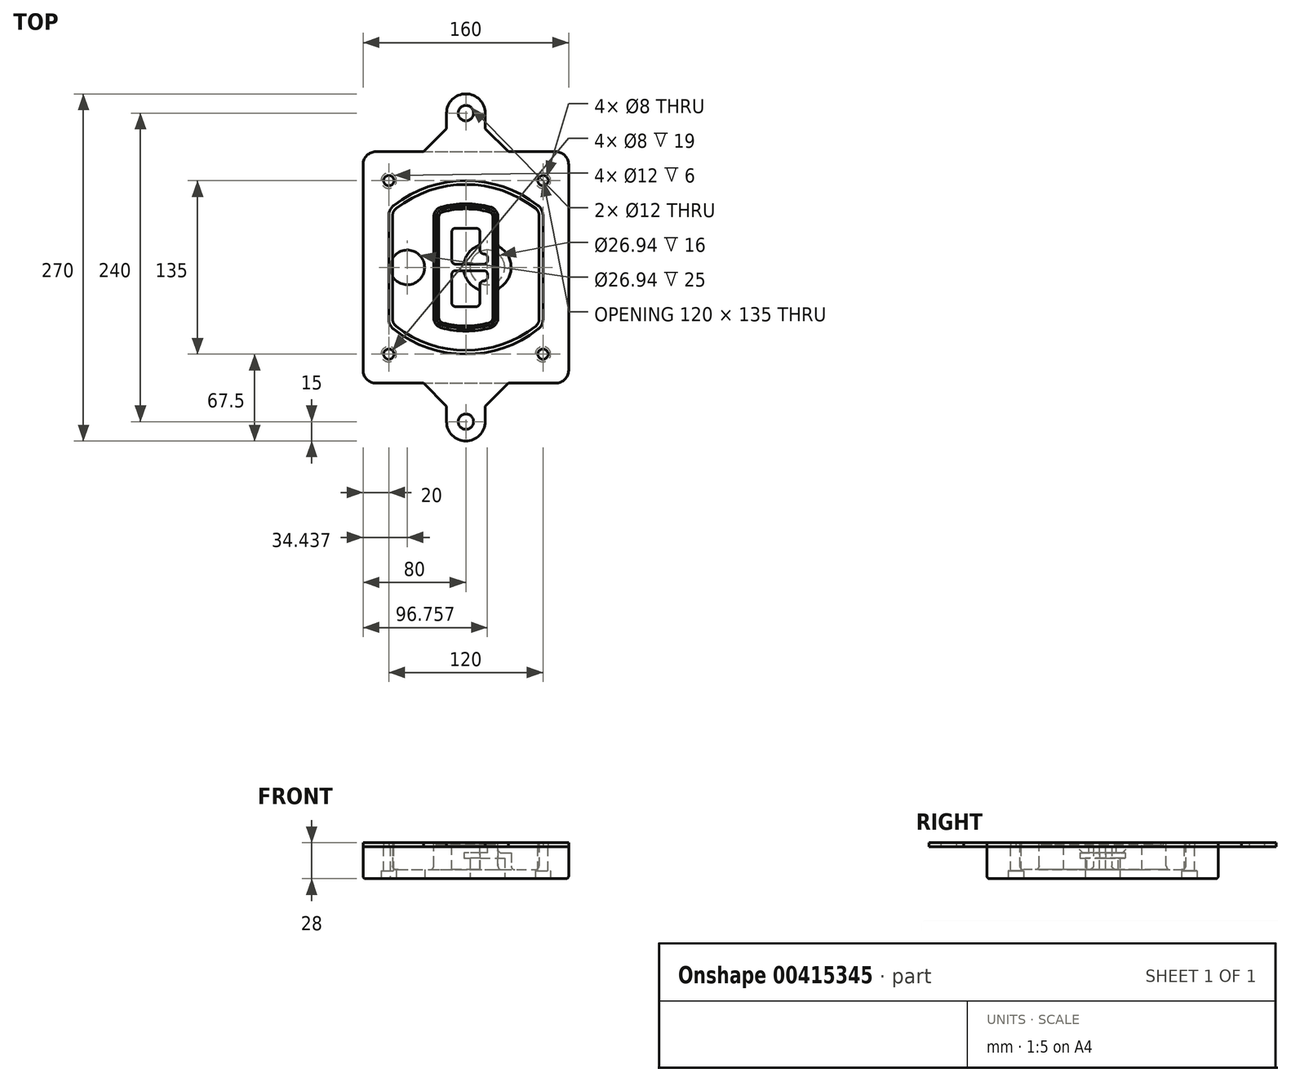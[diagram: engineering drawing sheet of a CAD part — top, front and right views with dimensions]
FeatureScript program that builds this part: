
annotation { "Feature Type Name" : "Feature", "Feature Type Description" : "" }
export const myFeature = defineFeature(function(context is Context, id is Id, definition is map)
    precondition{}
    {
        {
            var Q0;
            Q0=qCreatedBy(makeId("Top.planeOp"),FACE);
            var sketch = newSketch(context, id + "F0", { "sketchPlane" : qUnion([Q0])});
            skPoint(sketch, "E0.rect.middle", {"position": v(0, 0) * mm});
            skLineSegment(sketch, "E1.bottom", {"start": v(-70, -90) * mm, "end": v(70, -90) * mm});
            skLineSegment(sketch, "E1.top", {"start": v(-70, 90) * mm, "end": v(70, 90) * mm});
            skLineSegment(sketch, "E1.left", {"start": v(-80, -80) * mm, "end": v(-80, 80) * mm});
            skLineSegment(sketch, "E1.right", {"start": v(80, -80) * mm, "end": v(80, 80) * mm});
            skLineSegment(sketch, "E2", {"start": v(-80, 90) * mm, "end": v(80, -90) * mm, "construction": true});
            skLineSegment(sketch, "E3", {"start": v(80, 90) * mm, "end": v(-80, -90) * mm, "construction": true});
            skCircle(sketch, "E4", {"center": v(-60, 67.5) * mm, "radius": 4 * mm});
            skCircle(sketch, "E5", {"center": v(60, 67.5) * mm, "radius": 4 * mm});
            skCircle(sketch, "E6", {"center": v(60, -67.5) * mm, "radius": 4 * mm});
            skCircle(sketch, "E7", {"center": v(-60, -67.5) * mm, "radius": 4 * mm});
            skLineSegment(sketch, "E8", {"start": v(-60, 67.5) * mm, "end": v(60, 67.5) * mm, "construction": true});
            skLineSegment(sketch, "E9", {"start": v(60, 67.5) * mm, "end": v(60, -67.5) * mm, "construction": true});
            skLineSegment(sketch, "E10", {"start": v(60, -67.5) * mm, "end": v(-60, -67.5) * mm, "construction": true});
            skLineSegment(sketch, "E11", {"start": v(-60, -67.5) * mm, "end": v(-60, 67.5) * mm, "construction": true});
            skLineSegment(sketch, "E12", {"start": v(-60, 40.3) * mm, "end": v(-60, -40.3) * mm});
            skLineSegment(sketch, "E13", {"start": v(60, 40.3) * mm, "end": v(60, -40.3) * mm});
            skArc(sketch, "E14", {"start": v(56.15, 48.18) * mm, "mid": v(0, 67.5) * mm, "end": v(-56.15, 48.18) * mm});
            skArc(sketch, "E15", {"start": v(-56.15, -48.18) * mm, "mid": v(0, -67.5) * mm, "end": v(56.15, -48.18) * mm});
            skLineSegment(sketch, "E16", {"start": v(-60, 0) * mm, "end": v(60, 0) * mm, "construction": true});
            skPoint(sketch, "E17.visualSharp", {"position": v(-60, -45) * mm});
            skArc(sketch, "E17.filletArc", {"start": v(-60, -40.3) * mm, "mid": v(-58.99, -44.68) * mm, "end": v(-56.15, -48.18) * mm});
            skPoint(sketch, "E18.visualSharp", {"position": v(-60, 45) * mm});
            skArc(sketch, "E18.filletArc", {"start": v(-56.15, 48.18) * mm, "mid": v(-58.99, 44.68) * mm, "end": v(-60, 40.3) * mm});
            skPoint(sketch, "E19.visualSharp", {"position": v(60, 45) * mm});
            skArc(sketch, "E19.filletArc", {"start": v(60, 40.3) * mm, "mid": v(58.99, 44.68) * mm, "end": v(56.15, 48.18) * mm});
            skPoint(sketch, "E20.visualSharp", {"position": v(60, -45) * mm});
            skArc(sketch, "E20.filletArc", {"start": v(56.15, -48.18) * mm, "mid": v(58.99, -44.68) * mm, "end": v(60, -40.3) * mm});
            skPoint(sketch, "E21.visualSharp", {"position": v(-80, 90) * mm});
            skArc(sketch, "E21.filletArc", {"start": v(-70, 90) * mm, "mid": v(-77.07, 87.07) * mm, "end": v(-80, 80) * mm});
            skPoint(sketch, "E22.visualSharp", {"position": v(80, 90) * mm});
            skArc(sketch, "E22.filletArc", {"start": v(80, 80) * mm, "mid": v(77.07, 87.07) * mm, "end": v(70, 90) * mm});
            skPoint(sketch, "E23.visualSharp", {"position": v(80, -90) * mm});
            skArc(sketch, "E23.filletArc", {"start": v(70, -90) * mm, "mid": v(77.07, -87.07) * mm, "end": v(80, -80) * mm});
            skPoint(sketch, "E24.visualSharp", {"position": v(-80, -90) * mm});
            skArc(sketch, "E24.filletArc", {"start": v(-80, -80) * mm, "mid": v(-77.07, -87.07) * mm, "end": v(-70, -90) * mm});
            skArc(sketch, "E25.0", {"start": v(57, 40.3) * mm, "mid": v(56.3, 43.36) * mm, "end": v(54.3, 45.81) * mm});
            skLineSegment(sketch, "E25.1", {"start": v(57, 40.3) * mm, "end": v(57, -40.3) * mm});
            skArc(sketch, "E25.2", {"start": v(54.3, -45.81) * mm, "mid": v(56.3, -43.36) * mm, "end": v(57, -40.3) * mm});
            skArc(sketch, "E25.3", {"start": v(-54.3, -45.81) * mm, "mid": v(0, -64.5) * mm, "end": v(54.3, -45.81) * mm});
            skArc(sketch, "E25.4", {"start": v(-57, -40.3) * mm, "mid": v(-56.3, -43.36) * mm, "end": v(-54.3, -45.81) * mm});
            skArc(sketch, "E25.5", {"start": v(54.3, 45.81) * mm, "mid": v(0, 64.5) * mm, "end": v(-54.3, 45.81) * mm});
            skLineSegment(sketch, "E25.6", {"start": v(-57, 40.3) * mm, "end": v(-57, -40.3) * mm});
            skArc(sketch, "E25.7", {"start": v(-54.3, 45.81) * mm, "mid": v(-56.3, 43.36) * mm, "end": v(-57, 40.3) * mm});
            skArc(sketch, "E26.0", {"start": v(-58.62, 51.33) * mm, "mid": v(-62.58, 46.43) * mm, "end": v(-64, 40.3) * mm});
            skArc(sketch, "E26.1", {"start": v(58.62, 51.33) * mm, "mid": v(0, 71.5) * mm, "end": v(-58.62, 51.33) * mm});
            skArc(sketch, "E26.2", {"start": v(64, 40.3) * mm, "mid": v(62.58, 46.43) * mm, "end": v(58.62, 51.33) * mm});
            skLineSegment(sketch, "E26.3", {"start": v(64, 40.3) * mm, "end": v(64, -40.3) * mm});
            skArc(sketch, "E26.4", {"start": v(58.62, -51.33) * mm, "mid": v(62.58, -46.43) * mm, "end": v(64, -40.3) * mm});
            skLineSegment(sketch, "E26.5", {"start": v(-64, 40.3) * mm, "end": v(-64, -40.3) * mm});
            skArc(sketch, "E26.6", {"start": v(-58.62, -51.33) * mm, "mid": v(0, -71.5) * mm, "end": v(58.62, -51.33) * mm});
            skArc(sketch, "E26.7", {"start": v(-64, -40.3) * mm, "mid": v(-62.58, -46.43) * mm, "end": v(-58.62, -51.33) * mm});
            skSolve(sketch);
        }
        {
            var Q0;
            Q0=makeQuery(id+"F0.imprint","IMPRINT",FACE,{"disambiguationData":[TD([[makeQuery(id+"F0.imprint","IMPRINT",EDGE,{"derivedFrom":sQuery(id+"F0.wireOp",EDGE,"E1.bottom")}),1.0]])]});
            var Q1;
            Q1=makeQuery(id+"F0.imprint","IMPRINT",FACE,{"disambiguationData":[TD([[makeQuery(id+"F0.imprint","IMPRINT",EDGE,{"derivedFrom":sQuery(id+"F0.wireOp",EDGE,"E12")}),1.0]])]});
            var Q2;
            Q2=makeQuery(id+"F0.imprint","IMPRINT",FACE,{"disambiguationData":[TD([[makeQuery(id+"F0.imprint","IMPRINT",EDGE,{"derivedFrom":sQuery(id+"F0.wireOp",EDGE,"E25.0")}),1.0]])]});
            var Q3;
            Q3=makeQuery(id+"F0.imprint","IMPRINT",FACE,{"disambiguationData":[TD([[makeQuery(id+"F0.imprint","IMPRINT",EDGE,{"derivedFrom":sQuery(id+"F0.wireOp",EDGE,"E12")}),-1.0]])]});
            extrude(context, id + "F1", {"entities" : qUnion([Q0, Q1, Q2, Q3]), "oppositeDirection" : true, "depth" : 25 * mm});
        }
        {
            var Q0;
            Q0=makeQuery(id+"F0.imprint","IMPRINT",FACE,{"disambiguationData":[TD([[makeQuery(id+"F0.imprint","IMPRINT",EDGE,{"derivedFrom":sQuery(id+"F0.wireOp",EDGE,"E12")}),1.0]])]});
            extrude(context, id + "F2", {"entities" : qUnion([Q0]), "operationType" : NewBodyOperationType.ADD, "depth" : 3 * mm});
        }
        {
            var Q0;
            Q0=makeQuery(id+"F0.imprint","IMPRINT",FACE,{"disambiguationData":[TD([[makeQuery(id+"F0.imprint","IMPRINT",EDGE,{"derivedFrom":sQuery(id+"F0.wireOp",EDGE,"E25.0")}),1.0]])]});
            extrude(context, id + "F3", {"entities" : qUnion([Q0]), "operationType" : NewBodyOperationType.REMOVE, "oppositeDirection" : true, "depth" : 18 * mm});
        }
        {
            var Q0;
            Q0=makeQuery(id+"F2.opExtrude","CAP_FACE",FACE,{"disambiguationData":[OSD([sQuery(id+"F0.wireOp",EDGE,"E12"),sQuery(id+"F0.wireOp",EDGE,"E13"),sQuery(id+"F0.wireOp",EDGE,"E14"),sQuery(id+"F0.wireOp",EDGE,"E15"),sQuery(id+"F0.wireOp",EDGE,"E17.filletArc"),sQuery(id+"F0.wireOp",EDGE,"E18.filletArc"),sQuery(id+"F0.wireOp",EDGE,"E19.filletArc"),sQuery(id+"F0.wireOp",EDGE,"E20.filletArc"),sQuery(id+"F0.wireOp",EDGE,"E25.0"),sQuery(id+"F0.wireOp",EDGE,"E25.1"),sQuery(id+"F0.wireOp",EDGE,"E25.2"),sQuery(id+"F0.wireOp",EDGE,"E25.3"),sQuery(id+"F0.wireOp",EDGE,"E25.4"),sQuery(id+"F0.wireOp",EDGE,"E25.5"),sQuery(id+"F0.wireOp",EDGE,"E25.6"),sQuery(id+"F0.wireOp",EDGE,"E25.7")])],"isStart":false});
            var sketch = newSketch(context, id + "F4", { "sketchPlane" : qUnion([Q0])});
            skArc(sketch, "E27.0", {"start": v(-19.08, -46.97) * mm, "mid": v(0, -49.5) * mm, "end": v(19.08, -46.97) * mm});
            skArc(sketch, "E28.0", {"start": v(19.08, 46.97) * mm, "mid": v(0, 49.5) * mm, "end": v(-19.08, 46.97) * mm});
            skLineSegment(sketch, "E29", {"start": v(-25, 39.25) * mm, "end": v(-25, -39.25) * mm});
            skLineSegment(sketch, "E30", {"start": v(25, 39.25) * mm, "end": v(25, -39.25) * mm});
            skLineSegment(sketch, "E31", {"start": v(-25, 45.1) * mm, "end": v(25, 45.1) * mm, "construction": true});
            skLineSegment(sketch, "E32", {"start": v(-25, -45.1) * mm, "end": v(25, -45.1) * mm, "construction": true});
            skPoint(sketch, "E33.visualSharp", {"position": v(-25, 45.1) * mm});
            skArc(sketch, "E33.filletArc", {"start": v(-19.08, 46.97) * mm, "mid": v(-23.35, 44.11) * mm, "end": v(-25, 39.25) * mm});
            skPoint(sketch, "E34.visualSharp", {"position": v(25, 45.1) * mm});
            skArc(sketch, "E34.filletArc", {"start": v(25, 39.25) * mm, "mid": v(23.35, 44.11) * mm, "end": v(19.08, 46.97) * mm});
            skPoint(sketch, "E35.visualSharp", {"position": v(25, -45.1) * mm});
            skArc(sketch, "E35.filletArc", {"start": v(19.08, -46.97) * mm, "mid": v(23.35, -44.11) * mm, "end": v(25, -39.25) * mm});
            skPoint(sketch, "E36.visualSharp", {"position": v(-25, -45.1) * mm});
            skArc(sketch, "E36.filletArc", {"start": v(-25, -39.25) * mm, "mid": v(-23.35, -44.11) * mm, "end": v(-19.08, -46.97) * mm});
            skArc(sketch, "E37.0", {"start": v(54.3, 45.81) * mm, "mid": v(0, 64.5) * mm, "end": v(-54.3, 45.81) * mm});
            skArc(sketch, "E37.1", {"start": v(-54.3, 45.81) * mm, "mid": v(-56.3, 43.36) * mm, "end": v(-57, 40.3) * mm});
            skLineSegment(sketch, "E37.2", {"start": v(-57, 40.3) * mm, "end": v(-57, -40.3) * mm});
            skArc(sketch, "E37.3", {"start": v(-57, -40.3) * mm, "mid": v(-56.3, -43.36) * mm, "end": v(-54.3, -45.81) * mm});
            skArc(sketch, "E37.4", {"start": v(-54.3, -45.81) * mm, "mid": v(0, -64.5) * mm, "end": v(54.3, -45.81) * mm});
            skArc(sketch, "E37.5", {"start": v(54.3, -45.81) * mm, "mid": v(56.3, -43.36) * mm, "end": v(57, -40.3) * mm});
            skLineSegment(sketch, "E37.6", {"start": v(57, 40.3) * mm, "end": v(57, -40.3) * mm});
            skArc(sketch, "E37.7", {"start": v(57, 40.3) * mm, "mid": v(56.3, 43.36) * mm, "end": v(54.3, 45.81) * mm});
            skLineSegment(sketch, "E38.0", {"start": v(23, 39.25) * mm, "end": v(23, -39.25) * mm});
            skArc(sketch, "E38.1", {"start": v(18.56, -45.04) * mm, "mid": v(21.76, -42.9) * mm, "end": v(23, -39.25) * mm});
            skArc(sketch, "E38.2", {"start": v(-18.56, -45.04) * mm, "mid": v(0, -47.5) * mm, "end": v(18.56, -45.04) * mm});
            skArc(sketch, "E38.3", {"start": v(-23, -39.25) * mm, "mid": v(-21.76, -42.9) * mm, "end": v(-18.56, -45.04) * mm});
            skLineSegment(sketch, "E38.4", {"start": v(-23, 39.25) * mm, "end": v(-23, -39.25) * mm});
            skArc(sketch, "E38.5", {"start": v(23, 39.25) * mm, "mid": v(21.76, 42.9) * mm, "end": v(18.56, 45.04) * mm});
            skArc(sketch, "E38.6", {"start": v(-18.56, 45.04) * mm, "mid": v(-21.76, 42.9) * mm, "end": v(-23, 39.25) * mm});
            skArc(sketch, "E38.7", {"start": v(18.56, 45.04) * mm, "mid": v(0, 47.5) * mm, "end": v(-18.56, 45.04) * mm});
            skArc(sketch, "E39.0", {"start": v(21, 39.25) * mm, "mid": v(20.18, 41.68) * mm, "end": v(18.04, 43.1) * mm});
            skLineSegment(sketch, "E39.1", {"start": v(21, 39.25) * mm, "end": v(21, -39.25) * mm});
            skArc(sketch, "E39.2", {"start": v(18.04, -43.1) * mm, "mid": v(20.18, -41.68) * mm, "end": v(21, -39.25) * mm});
            skArc(sketch, "E39.3", {"start": v(-18.04, -43.1) * mm, "mid": v(0, -45.5) * mm, "end": v(18.04, -43.1) * mm});
            skArc(sketch, "E39.4", {"start": v(-21, -39.25) * mm, "mid": v(-20.18, -41.68) * mm, "end": v(-18.04, -43.1) * mm});
            skArc(sketch, "E39.5", {"start": v(18.04, 43.1) * mm, "mid": v(0, 45.5) * mm, "end": v(-18.04, 43.1) * mm});
            skLineSegment(sketch, "E39.6", {"start": v(-21, 39.25) * mm, "end": v(-21, -39.25) * mm});
            skArc(sketch, "E39.7", {"start": v(-18.04, 43.1) * mm, "mid": v(-20.18, 41.68) * mm, "end": v(-21, 39.25) * mm});
            skLineSegment(sketch, "E40", {"start": v(-25, 0) * mm, "end": v(25, 0) * mm, "construction": true});
            skLineSegment(sketch, "E41", {"start": v(-11, 5.5) * mm, "end": v(-11, 27.5) * mm});
            skLineSegment(sketch, "E42", {"start": v(-8, 30.5) * mm, "end": v(8, 30.5) * mm});
            skLineSegment(sketch, "E43", {"start": v(11, 27.5) * mm, "end": v(11, 13.5) * mm});
            skLineSegment(sketch, "E44", {"start": v(14, 10.5) * mm, "end": v(14, 10.5) * mm});
            skLineSegment(sketch, "E45", {"start": v(17, 7.5) * mm, "end": v(17, 5.5) * mm});
            skLineSegment(sketch, "E46", {"start": v(14, 2.5) * mm, "end": v(-8, 2.5) * mm});
            skPoint(sketch, "E47.visualSharp", {"position": v(-11, 30.5) * mm});
            skArc(sketch, "E47.filletArc", {"start": v(-8, 30.5) * mm, "mid": v(-10.12, 29.62) * mm, "end": v(-11, 27.5) * mm});
            skPoint(sketch, "E48.visualSharp", {"position": v(11, 30.5) * mm});
            skArc(sketch, "E48.filletArc", {"start": v(11, 27.5) * mm, "mid": v(10.12, 29.62) * mm, "end": v(8, 30.5) * mm});
            skPoint(sketch, "E49.visualSharp", {"position": v(11, 10.5) * mm});
            skArc(sketch, "E49.filletArc", {"start": v(11, 13.5) * mm, "mid": v(11.88, 11.38) * mm, "end": v(14, 10.5) * mm});
            skPoint(sketch, "E50.visualSharp", {"position": v(17, 10.5) * mm});
            skArc(sketch, "E50.filletArc", {"start": v(17, 7.5) * mm, "mid": v(16.12, 9.62) * mm, "end": v(14, 10.5) * mm});
            skPoint(sketch, "E51.visualSharp", {"position": v(17, 2.5) * mm});
            skArc(sketch, "E51.filletArc", {"start": v(14, 2.5) * mm, "mid": v(16.12, 3.38) * mm, "end": v(17, 5.5) * mm});
            skPoint(sketch, "E52.visualSharp", {"position": v(-11, 2.5) * mm});
            skArc(sketch, "E52.filletArc", {"start": v(-11, 5.5) * mm, "mid": v(-10.12, 3.38) * mm, "end": v(-8, 2.5) * mm});
            skLineSegment(sketch, "E53.0.MirrorCS", {"start": v(14, -2.5) * mm, "end": v(-8, -2.5) * mm});
            skArc(sketch, "E54.0.MirrorCS", {"start": v(-11, -5.5) * mm, "mid": v(-10.12, -3.38) * mm, "end": v(-8, -2.5) * mm});
            skLineSegment(sketch, "E55.0.MirrorCS", {"start": v(-11, -5.5) * mm, "end": v(-11, -27.5) * mm});
            skArc(sketch, "E56.0.MirrorCS", {"start": v(-8, -30.5) * mm, "mid": v(-10.12, -29.62) * mm, "end": v(-11, -27.5) * mm});
            skLineSegment(sketch, "E57.0.MirrorCS", {"start": v(-8, -30.5) * mm, "end": v(8, -30.5) * mm});
            skArc(sketch, "E58.0.MirrorCS", {"start": v(11, -27.5) * mm, "mid": v(10.12, -29.62) * mm, "end": v(8, -30.5) * mm});
            skLineSegment(sketch, "E59.0.MirrorCS", {"start": v(11, -27.5) * mm, "end": v(11, -13.5) * mm});
            skArc(sketch, "E60.0.MirrorCS", {"start": v(11, -13.5) * mm, "mid": v(11.88, -11.38) * mm, "end": v(14, -10.5) * mm});
            skArc(sketch, "E61.0.MirrorCS", {"start": v(17, -7.5) * mm, "mid": v(16.12, -9.62) * mm, "end": v(14, -10.5) * mm});
            skLineSegment(sketch, "E62.0.MirrorCS", {"start": v(17, -7.5) * mm, "end": v(17, -5.5) * mm});
            skArc(sketch, "E63.0.MirrorCS", {"start": v(14, -2.5) * mm, "mid": v(16.12, -3.38) * mm, "end": v(17, -5.5) * mm});
            skSolve(sketch);
        }
        {
            var Q0;
            Q0=makeQuery(id+"F4.imprint","IMPRINT",FACE,{"disambiguationData":[TD([[makeQuery(id+"F4.imprint","IMPRINT",EDGE,{"derivedFrom":sQuery(id+"F4.wireOp",EDGE,"E27.0")}),1.0]])]});
            var Q1;
            Q1=makeQuery(id+"F4.imprint","IMPRINT",FACE,{"disambiguationData":[TD([[makeQuery(id+"F4.imprint","IMPRINT",EDGE,{"derivedFrom":sQuery(id+"F4.wireOp",EDGE,"E38.0")}),-1.0]])]});
            var Q2;
            Q2=makeQuery(id+"F4.imprint","IMPRINT",FACE,{"disambiguationData":[TD([[makeQuery(id+"F4.imprint","IMPRINT",EDGE,{"derivedFrom":sQuery(id+"F4.wireOp",EDGE,"E39.0")}),1.0]])]});
            extrude(context, id + "F5", {"entities" : qUnion([Q0, Q1, Q2]), "operationType" : NewBodyOperationType.ADD, "endBound" : BoundingType.UP_TO_NEXT, "oppositeDirection" : true, "depth" : 25 * mm});
        }
        {
            var Q0;
            Q0=makeQuery(id+"F4.imprint","IMPRINT",FACE,{"disambiguationData":[TD([[makeQuery(id+"F4.imprint","IMPRINT",EDGE,{"derivedFrom":sQuery(id+"F4.wireOp",EDGE,"E38.0")}),-1.0]])]});
            extrude(context, id + "F6", {"entities" : qUnion([Q0]), "operationType" : NewBodyOperationType.REMOVE, "oppositeDirection" : true, "depth" : 2 * mm});
        }
        {
            var Q0;
            Q0=makeQuery(id+"F1.opExtrude","CAP_FACE",FACE,{"disambiguationData":[OSD([sQuery(id+"F0.wireOp",EDGE,"E1.bottom"),sQuery(id+"F0.wireOp",EDGE,"E1.top"),sQuery(id+"F0.wireOp",EDGE,"E1.left"),sQuery(id+"F0.wireOp",EDGE,"E1.right"),sQuery(id+"F0.wireOp",EDGE,"E4"),sQuery(id+"F0.wireOp",EDGE,"E5"),sQuery(id+"F0.wireOp",EDGE,"E6"),sQuery(id+"F0.wireOp",EDGE,"E7"),sQuery(id+"F0.wireOp",EDGE,"E21.filletArc"),sQuery(id+"F0.wireOp",EDGE,"E22.filletArc"),sQuery(id+"F0.wireOp",EDGE,"E23.filletArc"),sQuery(id+"F0.wireOp",EDGE,"E24.filletArc")])],"isStart":false});
            var sketch = newSketch(context, id + "F7", { "sketchPlane" : qUnion([Q0])});
            skCircle(sketch, "E64", {"center": v(16.76, 0) * mm, "radius": 13.47 * mm});
            skCircle(sketch, "E65", {"center": v(-45.56, 0) * mm, "radius": 13.47 * mm});
            skLineSegment(sketch, "E66", {"start": v(80, 0) * mm, "end": v(-80, 0) * mm});
            skCircle(sketch, "E67", {"center": v(16.76, 0) * mm, "radius": 18.47 * mm});
            skCircle(sketch, "E68", {"center": v(60, -67.5) * mm, "radius": 6 * mm});
            skCircle(sketch, "E69", {"center": v(-60, -67.5) * mm, "radius": 6 * mm});
            skCircle(sketch, "E70", {"center": v(-60, 67.5) * mm, "radius": 6 * mm});
            skCircle(sketch, "E71", {"center": v(60, 67.5) * mm, "radius": 6 * mm});
            skSolve(sketch);
        }
        {
            var Q0;
            {var subQ1=sQuery(id+"F7.wireOp",EDGE,"E66");var subQ4=sQuery(id+"F7.wireOp",EDGE,"E64");var subQ6=makeQuery(id+"F7.imprint","INTERSECT",VERTEX,{"disambiguationData":[OD(0.0)],"derivedFrom":[subQ4,subQ1]});Q0=makeQuery(id+"F7.imprint","IMPRINT",FACE,{"disambiguationData":[TD([[makeQuery(id+"F7.imprint","IMPRINT",EDGE,{"disambiguationData":[TD([[subQ6,-1.0]])],"derivedFrom":subQ4}),-1.0]])]});}
            var Q1;
            {var subQ0=sQuery(id+"F7.wireOp",EDGE,"E66");var subQ1=sQuery(id+"F7.wireOp",EDGE,"E64");var subQ3=makeQuery(id+"F7.imprint","INTERSECT",VERTEX,{"disambiguationData":[OD(0.0)],"derivedFrom":[subQ1,subQ0]});Q1=makeQuery(id+"F7.imprint","IMPRINT",FACE,{"disambiguationData":[TD([[makeQuery(id+"F7.imprint","IMPRINT",EDGE,{"disambiguationData":[TD([[subQ3,-1.0]])],"derivedFrom":subQ1}),1.0]])]});}
            var Q2;
            {var subQ0=sQuery(id+"F7.wireOp",EDGE,"E66");var subQ1=sQuery(id+"F7.wireOp",EDGE,"E64");var subQ3=makeQuery(id+"F7.imprint","INTERSECT",VERTEX,{"disambiguationData":[OD(0.0)],"derivedFrom":[subQ1,subQ0]});Q2=makeQuery(id+"F7.imprint","IMPRINT",FACE,{"disambiguationData":[TD([[makeQuery(id+"F7.imprint","IMPRINT",EDGE,{"disambiguationData":[TD([[subQ3,1.0]])],"derivedFrom":subQ1}),1.0]])]});}
            var Q3;
            {var subQ1=sQuery(id+"F7.wireOp",EDGE,"E66");var subQ4=sQuery(id+"F7.wireOp",EDGE,"E64");var subQ6=makeQuery(id+"F7.imprint","INTERSECT",VERTEX,{"disambiguationData":[OD(0.0)],"derivedFrom":[subQ4,subQ1]});Q3=makeQuery(id+"F7.imprint","IMPRINT",FACE,{"disambiguationData":[TD([[makeQuery(id+"F7.imprint","IMPRINT",EDGE,{"disambiguationData":[TD([[subQ6,1.0]])],"derivedFrom":subQ4}),-1.0]])]});}
            extrude(context, id + "F8", {"entities" : qUnion([Q0, Q1, Q2, Q3]), "operationType" : NewBodyOperationType.ADD, "oppositeDirection" : true, "depth" : 20 * mm});
        }
        {
            var Q0;
            {var subQ0=sQuery(id+"F7.wireOp",EDGE,"E66");var subQ1=sQuery(id+"F7.wireOp",EDGE,"E64");var subQ3=makeQuery(id+"F7.imprint","INTERSECT",VERTEX,{"disambiguationData":[OD(0.0)],"derivedFrom":[subQ1,subQ0]});Q0=makeQuery(id+"F7.imprint","IMPRINT",FACE,{"disambiguationData":[TD([[makeQuery(id+"F7.imprint","IMPRINT",EDGE,{"disambiguationData":[TD([[subQ3,-1.0]])],"derivedFrom":subQ1}),1.0]])]});}
            var Q1;
            {var subQ0=sQuery(id+"F7.wireOp",EDGE,"E66");var subQ1=sQuery(id+"F7.wireOp",EDGE,"E64");var subQ3=makeQuery(id+"F7.imprint","INTERSECT",VERTEX,{"disambiguationData":[OD(0.0)],"derivedFrom":[subQ1,subQ0]});Q1=makeQuery(id+"F7.imprint","IMPRINT",FACE,{"disambiguationData":[TD([[makeQuery(id+"F7.imprint","IMPRINT",EDGE,{"disambiguationData":[TD([[subQ3,1.0]])],"derivedFrom":subQ1}),1.0]])]});}
            extrude(context, id + "F9", {"entities" : qUnion([Q0, Q1]), "operationType" : NewBodyOperationType.REMOVE, "oppositeDirection" : true, "depth" : 16 * mm});
        }
        {
            var Q0;
            {var subQ0=sQuery(id+"F7.wireOp",EDGE,"E66");var subQ1=sQuery(id+"F7.wireOp",EDGE,"E65");var subQ3=makeQuery(id+"F7.imprint","INTERSECT",VERTEX,{"disambiguationData":[OD(0.0)],"derivedFrom":[subQ1,subQ0]});Q0=makeQuery(id+"F7.imprint","IMPRINT",FACE,{"disambiguationData":[TD([[makeQuery(id+"F7.imprint","IMPRINT",EDGE,{"disambiguationData":[TD([[subQ3,-1.0]])],"derivedFrom":subQ1}),1.0]])]});}
            var Q1;
            {var subQ0=sQuery(id+"F7.wireOp",EDGE,"E66");var subQ1=sQuery(id+"F7.wireOp",EDGE,"E65");var subQ3=makeQuery(id+"F7.imprint","INTERSECT",VERTEX,{"disambiguationData":[OD(0.0)],"derivedFrom":[subQ1,subQ0]});Q1=makeQuery(id+"F7.imprint","IMPRINT",FACE,{"disambiguationData":[TD([[makeQuery(id+"F7.imprint","IMPRINT",EDGE,{"disambiguationData":[TD([[subQ3,1.0]])],"derivedFrom":subQ1}),1.0]])]});}
            extrude(context, id + "F10", {"entities" : qUnion([Q0, Q1]), "operationType" : NewBodyOperationType.REMOVE, "oppositeDirection" : true, "depth" : 25 * mm});
        }
        {
            var Q0;
            Q0=makeQuery(id+"F7.imprint","IMPRINT",FACE,{"disambiguationData":[TD([[makeQuery(id+"F7.imprint","IMPRINT",EDGE,{"derivedFrom":sQuery(id+"F7.wireOp",EDGE,"E68")}),1.0]])]});
            var Q1;
            Q1=makeQuery(id+"F7.imprint","IMPRINT",FACE,{"disambiguationData":[TD([[makeQuery(id+"F7.imprint","IMPRINT",EDGE,{"derivedFrom":makeQuery(id+"F1.opExtrude","CAP_EDGE",EDGE,{"disambiguationData":[OSD([sQuery(id+"F0.wireOp",EDGE,"E5")])],"isStart":false})}),-1.0]])]});
            var Q2;
            Q2=makeQuery(id+"F7.imprint","IMPRINT",FACE,{"disambiguationData":[TD([[makeQuery(id+"F7.imprint","IMPRINT",EDGE,{"derivedFrom":sQuery(id+"F7.wireOp",EDGE,"E69")}),1.0]])]});
            var Q3;
            Q3=makeQuery(id+"F7.imprint","IMPRINT",FACE,{"disambiguationData":[TD([[makeQuery(id+"F7.imprint","IMPRINT",EDGE,{"derivedFrom":makeQuery(id+"F1.opExtrude","CAP_EDGE",EDGE,{"disambiguationData":[OSD([sQuery(id+"F0.wireOp",EDGE,"E4")])],"isStart":false})}),-1.0]])]});
            var Q4;
            Q4=makeQuery(id+"F7.imprint","IMPRINT",FACE,{"disambiguationData":[TD([[makeQuery(id+"F7.imprint","IMPRINT",EDGE,{"derivedFrom":sQuery(id+"F7.wireOp",EDGE,"E70")}),1.0]])]});
            var Q5;
            Q5=makeQuery(id+"F7.imprint","IMPRINT",FACE,{"disambiguationData":[TD([[makeQuery(id+"F7.imprint","IMPRINT",EDGE,{"derivedFrom":makeQuery(id+"F1.opExtrude","CAP_EDGE",EDGE,{"disambiguationData":[OSD([sQuery(id+"F0.wireOp",EDGE,"E7")])],"isStart":false})}),-1.0]])]});
            var Q6;
            Q6=makeQuery(id+"F7.imprint","IMPRINT",FACE,{"disambiguationData":[TD([[makeQuery(id+"F7.imprint","IMPRINT",EDGE,{"derivedFrom":sQuery(id+"F7.wireOp",EDGE,"E71")}),1.0]])]});
            var Q7;
            Q7=makeQuery(id+"F7.imprint","IMPRINT",FACE,{"disambiguationData":[TD([[makeQuery(id+"F7.imprint","IMPRINT",EDGE,{"derivedFrom":makeQuery(id+"F1.opExtrude","CAP_EDGE",EDGE,{"disambiguationData":[OSD([sQuery(id+"F0.wireOp",EDGE,"E6")])],"isStart":false})}),-1.0]])]});
            extrude(context, id + "F11", {"entities" : qUnion([Q0, Q1, Q2, Q3, Q4, Q5, Q6, Q7]), "operationType" : NewBodyOperationType.REMOVE, "oppositeDirection" : true, "depth" : 6 * mm});
        }
        {
            var Q0;
            Q0=makeQuery(id+"F9.boolean.opBoolean","COPY",FACE,{"derivedFrom":makeQuery(id+"F9.opExtrude","CAP_FACE",FACE,{"disambiguationData":[OSD([sQuery(id+"F7.wireOp",EDGE,"E64")])],"isStart":false})});
            var sketch = newSketch(context, id + "F12", { "sketchPlane" : qUnion([Q0])});
            skArc(sketch, "E72.0", {"start": v(11, 17.55) * mm, "mid": v(2.57, 11.82) * mm, "end": v(-1.54, 2.5) * mm});
            skArc(sketch, "E72.1", {"start": v(-1.54, -2.5) * mm, "mid": v(2.57, -11.82) * mm, "end": v(11, -17.55) * mm});
            skLineSegment(sketch, "E73", {"start": v(-1.54, -2.5) * mm, "end": v(14, -2.5) * mm});
            skLineSegment(sketch, "E74.0", {"start": v(14, 2.5) * mm, "end": v(-1.54, 2.5) * mm});
            skArc(sketch, "E74.1", {"start": v(14, 2.5) * mm, "mid": v(16.12, 3.38) * mm, "end": v(17, 5.5) * mm});
            skLineSegment(sketch, "E74.2", {"start": v(17, 7.5) * mm, "end": v(17, 5.5) * mm});
            skArc(sketch, "E74.3", {"start": v(17, 7.5) * mm, "mid": v(16.12, 9.62) * mm, "end": v(14, 10.5) * mm});
            skArc(sketch, "E74.4", {"start": v(11, 13.5) * mm, "mid": v(11.88, 11.38) * mm, "end": v(14, 10.5) * mm});
            skLineSegment(sketch, "E74.5", {"start": v(11, 17.55) * mm, "end": v(11, 13.5) * mm});
            skLineSegment(sketch, "E74.7", {"start": v(14, -2.5) * mm, "end": v(-1.54, -2.5) * mm});
            skArc(sketch, "E74.8", {"start": v(14, -2.5) * mm, "mid": v(16.12, -3.38) * mm, "end": v(17, -5.5) * mm});
            skLineSegment(sketch, "E74.9", {"start": v(17, -7.5) * mm, "end": v(17, -5.5) * mm});
            skArc(sketch, "E74.10", {"start": v(17, -7.5) * mm, "mid": v(16.12, -9.62) * mm, "end": v(14, -10.5) * mm});
            skArc(sketch, "E74.11", {"start": v(11, -13.5) * mm, "mid": v(11.88, -11.38) * mm, "end": v(14, -10.5) * mm});
            skLineSegment(sketch, "E74.12", {"start": v(11, -17.55) * mm, "end": v(11, -13.5) * mm});
            skPoint(sketch, "E75.orphan", {"position": v(11, -27.5) * mm});
            skPoint(sketch, "E76.orphan", {"position": v(-8, -2.5) * mm});
            skPoint(sketch, "E77.orphan", {"position": v(-8, 2.5) * mm});
            skPoint(sketch, "E78.orphan", {"position": v(11, 27.5) * mm});
            skSolve(sketch);
        }
        {
            var Q0;
            {var subQ7=sQuery(id+"F12.wireOp",EDGE,"E72.0");var subQ14=sQuery(id+"F12.wireOp",EDGE,"E72.1");var subQ16=sQuery(id+"F12.wireOp",EDGE,"E74.1");var subQ18=sQuery(id+"F12.wireOp",EDGE,"E74.8");Q0=qUnion([makeQuery(id+"F12.imprint","IMPRINT",FACE,{"disambiguationData":[TD([[makeQuery(id+"F12.imprint","IMPRINT",EDGE,{"derivedFrom":subQ7}),1.0]])]}),makeQuery(id+"F12.imprint","IMPRINT",FACE,{"disambiguationData":[TD([[makeQuery(id+"F12.imprint","IMPRINT",EDGE,{"derivedFrom":subQ14}),1.0]])]}),makeQuery(id+"F12.imprint","IMPRINT",FACE,{"disambiguationData":[TD([[makeQuery(id+"F12.imprint","IMPRINT",EDGE,{"derivedFrom":subQ16}),1.0]])]}),makeQuery(id+"F12.imprint","IMPRINT",FACE,{"disambiguationData":[TD([[makeQuery(id+"F12.imprint","IMPRINT",EDGE,{"derivedFrom":subQ18}),-1.0]])]})]);}
            var Q1;
            Q1=makeQuery(id+"F5.boolean.opBoolean","SPLIT",FACE,{"disambiguationData":[TD([makeQuery(id+"F5.opExtrude","SWEPT_FACE",FACE,{"disambiguationData":[OSD([sQuery(id+"F4.wireOp",EDGE,"E41")])]})])],"derivedFrom":makeQuery(id+"F3.boolean.opBoolean","COPY",FACE,{"derivedFrom":makeQuery(id+"F3.opExtrude","CAP_FACE",FACE,{"disambiguationData":[OSD([sQuery(id+"F0.wireOp",EDGE,"E25.0"),sQuery(id+"F0.wireOp",EDGE,"E25.1"),sQuery(id+"F0.wireOp",EDGE,"E25.2"),sQuery(id+"F0.wireOp",EDGE,"E25.3"),sQuery(id+"F0.wireOp",EDGE,"E25.4"),sQuery(id+"F0.wireOp",EDGE,"E25.5"),sQuery(id+"F0.wireOp",EDGE,"E25.6"),sQuery(id+"F0.wireOp",EDGE,"E25.7")])],"isStart":false})})});
            extrude(context, id + "F13", {"entities" : qUnion([Q0]), "operationType" : NewBodyOperationType.REMOVE, "endBound" : BoundingType.UP_TO_SURFACE, "endBoundEntityFace" : qUnion([Q1]), "depth" : 25 * mm});
        }
        {
            var Q0;
            Q0=makeQuery(id+"F3.boolean.opBoolean","COPY",EDGE,{"derivedFrom":makeQuery(id+"F3.opExtrude","CAP_EDGE",EDGE,{"disambiguationData":[OSD([sQuery(id+"F0.wireOp",EDGE,"E25.6")])],"isStart":false})});
            var Q1;
            Q1=makeQuery(id+"F8.boolean.opBoolean","INTERSECT",EDGE,{"derivedFrom":[makeQuery(id+"F5.opExtrude","SWEPT_FACE",FACE,{"disambiguationData":[OSD([sQuery(id+"F4.wireOp",EDGE,"E30")])]}),makeQuery(id+"F8.opExtrude","CAP_FACE",FACE,{"disambiguationData":[OSD([sQuery(id+"F7.wireOp",EDGE,"E67")])],"isStart":false})]});
            var Q2;
            Q2=makeQuery(id+"F8.boolean.opBoolean","INTERSECT",EDGE,{"disambiguationData":[OD(1.0)],"derivedFrom":[makeQuery(id+"F5.opExtrude","SWEPT_FACE",FACE,{"disambiguationData":[OSD([sQuery(id+"F4.wireOp",EDGE,"E30")])]}),makeQuery(id+"F8.opExtrude","SWEPT_FACE",FACE,{"disambiguationData":[OSD([sQuery(id+"F7.wireOp",EDGE,"E67")])]})]});
            var Q3;
            {var subQ0=sQuery(id+"F4.wireOp",EDGE,"E30");Q3=makeQuery(id+"F8.boolean.opBoolean","SPLIT",EDGE,{"disambiguationData":[TD([makeQuery(id+"F5.opExtrude","SWEPT_FACE",FACE,{"disambiguationData":[OSD([sQuery(id+"F4.wireOp",EDGE,"E35.filletArc")])]})])],"derivedFrom":makeQuery(id+"F5.opExtrude","CAP_EDGE",EDGE,{"disambiguationData":[OSD([subQ0])],"isStart":false})});}
            var Q4;
            {var subQ0=sQuery(id+"F0.wireOp",EDGE,"E25.7");var subQ1=sQuery(id+"F0.wireOp",EDGE,"E25.1");var subQ2=sQuery(id+"F0.wireOp",EDGE,"E25.6");var subQ3=sQuery(id+"F0.wireOp",EDGE,"E25.5");var subQ4=sQuery(id+"F0.wireOp",EDGE,"E25.4");var subQ5=sQuery(id+"F0.wireOp",EDGE,"E25.0");var subQ6=sQuery(id+"F0.wireOp",EDGE,"E25.2");var subQ7=sQuery(id+"F0.wireOp",EDGE,"E25.3");Q4=makeQuery(id+"F8.boolean.opBoolean","INTERSECT",EDGE,{"derivedFrom":[makeQuery(id+"F5.boolean.opBoolean","SPLIT",FACE,{"disambiguationData":[TD([makeQuery(id+"F2.opExtrude","SWEPT_FACE",FACE,{"disambiguationData":[OSD([subQ5])]})])],"derivedFrom":makeQuery(id+"F3.boolean.opBoolean","COPY",FACE,{"derivedFrom":makeQuery(id+"F3.opExtrude","CAP_FACE",FACE,{"disambiguationData":[OSD([subQ5,subQ1,subQ6,subQ7,subQ4,subQ3,subQ2,subQ0])],"isStart":false})})}),makeQuery(id+"F8.opExtrude","SWEPT_FACE",FACE,{"disambiguationData":[OSD([sQuery(id+"F7.wireOp",EDGE,"E67")])]})]});}
            var Q5;
            Q5=makeQuery(id+"F8.boolean.opBoolean","INTERSECT",EDGE,{"disambiguationData":[OD(0.0)],"derivedFrom":[makeQuery(id+"F5.opExtrude","SWEPT_FACE",FACE,{"disambiguationData":[OSD([sQuery(id+"F4.wireOp",EDGE,"E30")])]}),makeQuery(id+"F8.opExtrude","SWEPT_FACE",FACE,{"disambiguationData":[OSD([sQuery(id+"F7.wireOp",EDGE,"E67")])]})]});
            fillet(context, id + "F14", {"entities" : qUnion([Q0, Q1, Q2, Q3, Q4, Q5]), "radius" : 3 * mm, "tangentPropagation" : true, "allowEdgeOverflow" : false});
        }
        {
            var Q0;
            Q0=makeQuery(id+"F1.opExtrude","CAP_EDGE",EDGE,{"disambiguationData":[OSD([sQuery(id+"F0.wireOp",EDGE,"E1.bottom")])],"isStart":false});
            fillet(context, id + "F15", {"entities" : qUnion([Q0]), "radius" : 2 * mm, "tangentPropagation" : true, "allowEdgeOverflow" : false});
        }
        {
            var Q0;
            {var subQ0=sQuery(id+"F0.wireOp",EDGE,"E21.filletArc");var subQ1=sQuery(id+"F0.wireOp",EDGE,"E7");var subQ2=sQuery(id+"F0.wireOp",EDGE,"E6");var subQ3=sQuery(id+"F0.wireOp",EDGE,"E5");var subQ4=sQuery(id+"F0.wireOp",EDGE,"E4");var subQ5=sQuery(id+"F0.wireOp",EDGE,"E22.filletArc");var subQ6=sQuery(id+"F0.wireOp",EDGE,"E1.bottom");var subQ7=sQuery(id+"F0.wireOp",EDGE,"E1.right");var subQ8=sQuery(id+"F0.wireOp",EDGE,"E1.top");var subQ9=sQuery(id+"F0.wireOp",EDGE,"E1.left");var subQ10=sQuery(id+"F0.wireOp",EDGE,"E23.filletArc");var subQ11=sQuery(id+"F0.wireOp",EDGE,"E24.filletArc");Q0=makeQuery(id+"F2.boolean.opBoolean","SPLIT",FACE,{"disambiguationData":[TD([makeQuery(id+"F1.opExtrude","SWEPT_FACE",FACE,{"disambiguationData":[OSD([subQ6])]})])],"derivedFrom":makeQuery(id+"F1.opExtrude","CAP_FACE",FACE,{"disambiguationData":[OSD([subQ6,subQ8,subQ9,subQ7,subQ4,subQ3,subQ2,subQ1,subQ0,subQ5,subQ10,subQ11])],"isStart":true})});}
            var sketch = newSketch(context, id + "F16", { "sketchPlane" : qUnion([Q0])});
            skCircle(sketch, "E79.0", {"center": v(-60, 67.5) * mm, "radius": 4 * mm});
            skCircle(sketch, "E80.0", {"center": v(60, 67.5) * mm, "radius": 4 * mm});
            skArc(sketch, "E81.0", {"start": v(56.15, 48.18) * mm, "mid": v(0, 67.5) * mm, "end": v(-56.15, 48.18) * mm});
            skArc(sketch, "E82.0", {"start": v(60, 40.3) * mm, "mid": v(58.99, 44.68) * mm, "end": v(56.15, 48.18) * mm});
            skLineSegment(sketch, "E83.0", {"start": v(60, 40.3) * mm, "end": v(60, -40.3) * mm});
            skArc(sketch, "E84.0", {"start": v(56.15, -48.18) * mm, "mid": v(58.99, -44.68) * mm, "end": v(60, -40.3) * mm});
            skArc(sketch, "E85.0", {"start": v(-56.15, -48.18) * mm, "mid": v(0, -67.5) * mm, "end": v(56.15, -48.18) * mm});
            skArc(sketch, "E86.0", {"start": v(-60, -40.3) * mm, "mid": v(-58.99, -44.68) * mm, "end": v(-56.15, -48.18) * mm});
            skLineSegment(sketch, "E87.0", {"start": v(-60, 40.3) * mm, "end": v(-60, -40.3) * mm});
            skArc(sketch, "E88.0", {"start": v(-56.15, 48.18) * mm, "mid": v(-58.99, 44.68) * mm, "end": v(-60, 40.3) * mm});
            skCircle(sketch, "E89.0", {"center": v(-60, -67.5) * mm, "radius": 4 * mm});
            skCircle(sketch, "E90.0", {"center": v(60, -67.5) * mm, "radius": 4 * mm});
            skLineSegment(sketch, "E91.0", {"start": v(-70, -90) * mm, "end": v(70, -90) * mm});
            skArc(sketch, "E92.0", {"start": v(70, -90) * mm, "mid": v(77.07, -87.07) * mm, "end": v(80, -80) * mm});
            skArc(sketch, "E93.0", {"start": v(-80, -80) * mm, "mid": v(-77.07, -87.07) * mm, "end": v(-70, -90) * mm});
            skLineSegment(sketch, "E94.0", {"start": v(-80, -80) * mm, "end": v(-80, 80) * mm});
            skLineSegment(sketch, "E95.0", {"start": v(80, -80) * mm, "end": v(80, 80) * mm});
            skArc(sketch, "E96.0", {"start": v(80, 80) * mm, "mid": v(77.07, 87.07) * mm, "end": v(70, 90) * mm});
            skArc(sketch, "E97.0", {"start": v(-70, 90) * mm, "mid": v(-77.07, 87.07) * mm, "end": v(-80, 80) * mm});
            skLineSegment(sketch, "E98.0", {"start": v(70, 90) * mm, "end": v(-70, 90) * mm});
            skLineSegment(sketch, "E99", {"start": v(0, 90) * mm, "end": v(0, 120) * mm, "construction": true});
            skPoint(sketch, "E99.endSnap0", {"position": v(0, 90) * mm});
            skLineSegment(sketch, "E100", {"start": v(-33, 90) * mm, "end": v(-15, 108) * mm});
            skLineSegment(sketch, "E101", {"start": v(-80, 0) * mm, "end": v(80, 0) * mm, "construction": true});
            skPoint(sketch, "E102.MirrorP", {"position": v(0, -90) * mm});
            skLineSegment(sketch, "E103", {"start": v(-15, 108) * mm, "end": v(-15, 120) * mm});
            skLineSegment(sketch, "E104.MirrorCS", {"start": v(33, 90) * mm, "end": v(15, 108) * mm});
            skLineSegment(sketch, "E105.MirrorCS", {"start": v(15, 108) * mm, "end": v(15, 120) * mm});
            skArc(sketch, "E106", {"start": v(-15, 120) * mm, "mid": v(0, 135) * mm, "end": v(15, 120) * mm});
            skCircle(sketch, "E107", {"center": v(0, 120) * mm, "radius": 6 * mm});
            skCircle(sketch, "E108.MirrorC", {"center": v(0, -120) * mm, "radius": 6 * mm});
            skLineSegment(sketch, "E109.MirrorCS", {"start": v(-33, -90) * mm, "end": v(-15, -108) * mm});
            skLineSegment(sketch, "E110.MirrorCS", {"start": v(-15, -108) * mm, "end": v(-15, -120) * mm});
            skLineSegment(sketch, "E111.MirrorCS", {"start": v(15, -108) * mm, "end": v(15, -120) * mm});
            skLineSegment(sketch, "E112.MirrorCS", {"start": v(33, -90) * mm, "end": v(15, -108) * mm});
            skArc(sketch, "E113.MirrorCS", {"start": v(-15, -120) * mm, "mid": v(0, -135) * mm, "end": v(15, -120) * mm});
            skSolve(sketch);
        }
        {
            var Q0;
            Q0 = qSketchRegion(id + "F16", true);
            var Q1;
            Q1=makeQuery(id+"F2.opExtrude","CAP_FACE",FACE,{"disambiguationData":[OSD([sQuery(id+"F0.wireOp",EDGE,"E12"),sQuery(id+"F0.wireOp",EDGE,"E13"),sQuery(id+"F0.wireOp",EDGE,"E14"),sQuery(id+"F0.wireOp",EDGE,"E15"),sQuery(id+"F0.wireOp",EDGE,"E17.filletArc"),sQuery(id+"F0.wireOp",EDGE,"E18.filletArc"),sQuery(id+"F0.wireOp",EDGE,"E19.filletArc"),sQuery(id+"F0.wireOp",EDGE,"E20.filletArc"),sQuery(id+"F0.wireOp",EDGE,"E25.0"),sQuery(id+"F0.wireOp",EDGE,"E25.1"),sQuery(id+"F0.wireOp",EDGE,"E25.2"),sQuery(id+"F0.wireOp",EDGE,"E25.3"),sQuery(id+"F0.wireOp",EDGE,"E25.4"),sQuery(id+"F0.wireOp",EDGE,"E25.5"),sQuery(id+"F0.wireOp",EDGE,"E25.6"),sQuery(id+"F0.wireOp",EDGE,"E25.7")])],"isStart":false});
            extrude(context, id + "F17", {"entities" : qUnion([Q0]), "endBound" : BoundingType.UP_TO_SURFACE, "endBoundEntityFace" : qUnion([Q1]), "depth" : 25 * mm});
        }
    });
